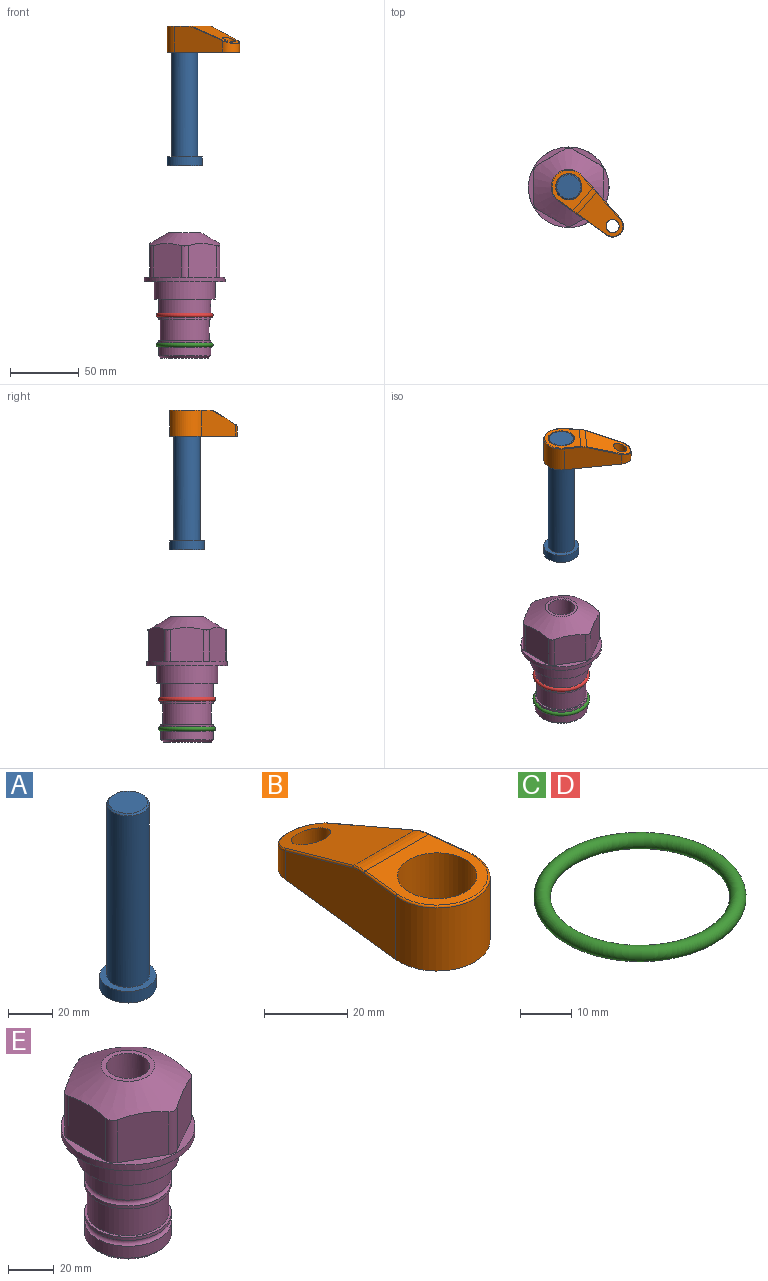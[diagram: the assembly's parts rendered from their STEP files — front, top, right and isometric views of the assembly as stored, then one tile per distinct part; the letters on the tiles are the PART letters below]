
ASSEMBLY  parts=5 mates=3
PART A: 6 faces, bbox 25.4x25.4x101.6 mm
  f0: plane 17.46x17.46mm, normal (0,0,1), area 239.5mm2, adj f5
  f1: plane 25.4x25.4mm, normal (0,0,-1), area 506.7mm2, adj f2
  f2: cylinder r=12.7mm len=25.4mm, axis (0,0,1), area 506.7mm2, adj f1,f3
  f3: plane 25.4x25.4mm, normal (0,0,1), area 221.7mm2, adj f2,f4
  f4: cylinder r=9.53mm len=94.46mm, axis (0,0,1), area 5653mm2, adj f3,f5
  f5: cone r=8.73mm half-angle=45deg, axis (0,0,-1), area 64.4mm2, adj f0,f4
PART B: 44 faces, bbox 27.5x64.5x19.1 mm
  f0: plane 2.3x0.95mm, normal (0,0,-1), area 1mm2, adj f25,f30,f34
  f1: plane 63.5x25.4mm, normal (0,0,-1), area 561.7mm2, adj f2,f3,f4,f5,f6,f7,f19,f20
  f2: cylinder r=12.7mm len=25.4mm, axis (0,0,-1), area 792.2mm2, adj f1,f3,f5,f13
  f3: plane 42.33x18.54mm, normal (0.99,0.11,0), area 647mm2, adj f1,f2,f4,f11,f12,f14
  f4: cylinder r=7.94mm len=15.78mm, axis (0,0,-1), area 158.6mm2, adj f1,f3,f5,f16
  f5: plane 42.33x18.54mm, normal (-0.99,0.11,0), area 647mm2, adj f1,f2,f4,f15,f17,f18
  f6: cylinder r=9.53mm len=19.05mm, axis (0,0,-1), area 1140.1mm2, adj f1,f8
  f7: cylinder r=4.76mm len=10.98mm, axis (0,0,-1), area 276.1mm2, adj f1,f9
  f8: plane 25.83x24.38mm, normal (0,0,1), area 262.2mm2, adj f6,f10,f11,f13,f15
  f9: plane 32.49x20.55mm, normal (0,0.34,0.94), area 489.9mm2, adj f7,f10,f14,f16,f18
  f10: cylinder r=12.7mm len=21.49mm, axis (-1,0,0), area 93.2mm2, adj f8,f9,f12,f17
  f11: cylinder r=0.51mm len=12.34mm, axis (0.11,-0.99,0), area 9.9mm2, adj f3,f8,f12,f13
  f12: bspline ~7.62x1.64mm, area 3.5mm2, adj f3,f10,f11,f14
  f13: torus R=12.19mm, axis (0,0,1), area 33.6mm2, adj f2,f8,f11,f15
  f14: cylinder r=0.51mm len=26.01mm, axis (0.1,-0.93,0.34), area 21.6mm2, adj f3,f9,f12,f16
  f15: cylinder r=0.51mm len=12.34mm, axis (0.11,0.99,0), area 9.9mm2, adj f5,f8,f13,f17
  f16: bspline ~15.78x7.05mm, area 15.7mm2, adj f4,f9,f14,f18
  f17: bspline ~7.62x1.64mm, area 3.5mm2, adj f5,f10,f15,f18
  f18: cylinder r=0.51mm len=26.01mm, axis (0.1,0.93,-0.34), area 21.6mm2, adj f5,f9,f16,f17
  f19: plane 21.6x14.29mm, normal (-0.99,-0.11,0), area 242.6mm2, adj f1,f26,f28,f34,f36,f38
  f20: plane 21.6x14.29mm, normal (0.99,-0.11,0), area 242.6mm2, adj f1,f27,f29,f37,f39,f41
  f21: cylinder r=12.7mm len=14.29mm, axis (0,0,-1), area 173.2mm2, adj f1,f26,f27,f30,f31,f33
  f22: cylinder r=7.94mm len=7.63mm, axis (0,0,-1), area 53.8mm2, adj f1,f28,f29,f42
  f23: plane 2.3x0.95mm, normal (0,0,-1), area 1mm2, adj f25,f33,f37
  f24: plane 17.94x12.32mm, normal (0,-0.34,-0.94), area 191.2mm2, adj f25,f38,f41,f42
  f25: cylinder r=9.53mm len=12.93mm, axis (-1,0,0), area 37.5mm2, adj f0,f23,f24,f31,f36,f39
  f26: cylinder r=1.59mm len=14.29mm, axis (0,0,-1), area 49mm2, adj f1,f19,f21,f32
  f27: cylinder r=1.59mm len=14.29mm, axis (0,0,-1), area 49mm2, adj f1,f20,f21,f35
  f28: cylinder r=1.59mm len=7.28mm, axis (0,0,-1), area 22.1mm2, adj f1,f19,f22,f40
  f29: cylinder r=1.59mm len=7.28mm, axis (0,0,-1), area 22.1mm2, adj f1,f20,f22,f43
  f30: torus R=14.29mm, axis (0,0,1), area 5.8mm2, adj f0,f21,f31,f32
  f31: bspline ~11.06x2.73mm, area 20.8mm2, adj f21,f25,f30,f33
  f32: sphere r=1.59mm, area 5.4mm2, adj f26,f30,f34
  f33: torus R=14.29mm, axis (0,0,1), area 5.8mm2, adj f21,f23,f31,f35
  f34: cylinder r=1.59mm len=1.68mm, axis (-0.11,0.99,0), area 2.4mm2, adj f0,f19,f32,f36
  f35: sphere r=1.59mm, area 5.4mm2, adj f27,f33,f37
  f36: bspline ~5.82x2.33mm, area 7.7mm2, adj f19,f25,f34,f38
  f37: cylinder r=1.59mm len=1.68mm, axis (0.11,0.99,0), area 2.4mm2, adj f20,f23,f35,f39
  f38: cylinder r=1.59mm len=18.33mm, axis (0.1,-0.93,0.34), area 46.7mm2, adj f19,f24,f36,f40
  f39: bspline ~5.82x2.33mm, area 7.7mm2, adj f20,f25,f37,f41
  f40: sphere r=1.59mm, area 3.6mm2, adj f28,f38,f42
  f41: cylinder r=1.59mm len=18.33mm, axis (0.1,0.93,-0.34), area 46.7mm2, adj f20,f24,f39,f43
  f42: bspline ~8.31x1.84mm, area 15.3mm2, adj f22,f24,f40,f43
  f43: sphere r=1.59mm, area 3.6mm2, adj f29,f41,f42
PART C: 1 faces, bbox 44.7x44.7x3.2 mm
  f0: torus R=19.05mm, axis (0,0,1), area 1193.9mm2
PART D: same geometry as C
PART E: 36 faces, bbox 58.7x58.7x91.2 mm
  f0: cylinder r=17.78mm len=35.56mm, axis (0,0,1), area 1670.8mm2, adj f23,f24,f31
  f1: cylinder r=19.05mm len=38.1mm, axis (0,0,1), area 1191.9mm2, adj f26,f27,f30
  f2: plane 58.66x58.66mm, normal (0,0,-1), area 1150.6mm2, adj f3,f28
  f3: cylinder r=29.33mm len=58.66mm, axis (0,0,-1), area 585.1mm2, adj f2,f4
  f4: plane 58.66x58.66mm, normal (0,0,1), area 475.9mm2, adj f3,f5,f6,f7,f8,f9,f10,f11
  f5: plane 24.5x20.32mm, normal (-0.5,0.87,0), area 562.8mm2, adj f4,f15,f16,f17
  f6: plane 24.5x20.32mm, normal (0.5,0.87,0), area 562.8mm2, adj f4,f14,f15,f17
  f7: plane 24.5x23.48mm, normal (1,0,0), area 562.8mm2, adj f4,f13,f14,f17
  f8: plane 24.5x20.32mm, normal (0.5,-0.87,0), area 562.8mm2, adj f4,f12,f13,f17
  f9: plane 24.5x20.32mm, normal (-0.5,-0.87,0), area 562.8mm2, adj f4,f11,f12,f17
  f10: plane 24.5x23.48mm, normal (-1,0,0), area 562.8mm2, adj f4,f11,f16,f17
  f11: cylinder r=5.08mm len=23.01mm, axis (0,0,-1), area 121.2mm2, adj f4,f9,f10,f17
  f12: cylinder r=5.08mm len=23.01mm, axis (0,0,-1), area 121.2mm2, adj f4,f8,f9,f17
  f13: cylinder r=5.08mm len=23.01mm, axis (0,0,-1), area 121.2mm2, adj f4,f7,f8,f17
  f14: cylinder r=5.08mm len=23.01mm, axis (0,0,-1), area 121.2mm2, adj f4,f6,f7,f17
  f15: cylinder r=5.08mm len=23.01mm, axis (0,0,-1), area 121.2mm2, adj f4,f5,f6,f17
  f16: cylinder r=5.08mm len=23.01mm, axis (0,0,-1), area 121.2mm2, adj f4,f5,f10,f17
  f17: cone r=11.73mm half-angle=60deg, axis (0,0,-1), area 2071.8mm2, adj f5,f6,f7,f8,f9,f10,f11,f12
  f18: plane 23.46x23.46mm, normal (0,0,1), area 147.4mm2, adj f17,f35
  f19: plane 34.93x34.93mm, normal (0,0,-1), area 958mm2, adj f29
  f20: cylinder r=19.05mm len=38.1mm, axis (0,0,1), area 760.1mm2, adj f21,f29
  f21: torus R=19.05mm, axis (0,0,1), area 565.3mm2, adj f20,f22
  f22: cylinder r=19.05mm len=38.1mm, axis (0,0,1), area 190mm2, adj f21,f23
  f23: plane 38.1x38.1mm, normal (0,0,1), area 146.9mm2, adj f0,f22
  f24: plane 38.1x38.1mm, normal (0,0,-1), area 146.9mm2, adj f0,f25
  f25: cylinder r=19.05mm len=38.1mm, axis (0,0,1), area 190mm2, adj f24,f26
  f26: torus R=19.05mm, axis (0,0,1), area 565.3mm2, adj f1,f25
  f27: plane 44.45x44.45mm, normal (0,0,-1), area 411.7mm2, adj f1,f28
  f28: cylinder r=22.23mm len=44.45mm, axis (0,0,1), area 1773.5mm2, adj f2,f27
  f29: cone r=19.05mm half-angle=45deg, axis (0,0,1), area 257.5mm2, adj f19,f20
  f30: cylinder r=3.17mm len=6.75mm, axis (-1,0,0), area 128mm2, adj f1,f33
  f31: cylinder r=3.17mm len=6.35mm, axis (-1,0,0), area 102.5mm2, adj f0,f33
  f32: plane 25.4x25.4mm, normal (0,0,1), area 506.7mm2, adj f33
  f33: cylinder r=12.7mm len=66.42mm, axis (0,0,-1), area 5236.2mm2, adj f30,f31,f32,f34
  f34: cone r=9.53mm half-angle=30deg, axis (0,0,-1), area 443.4mm2, adj f33,f35
  f35: cylinder r=9.53mm len=19.05mm, axis (0,0,-1), area 849mm2, adj f18,f34
PLACE A rot(axis=(0,0,-1),41.8deg) t=(0,0,112.27)mm
PLACE B rot(axis=(0,0,-1),131.8deg) t=(0,0,166.88)mm
PLACE C t=(0,0,-21.59)mm
PLACE D at identity
PLACE E at identity fixed
MATE fastened C.f0 <-> E.f0  axis (0,0,1) through (0,0,-46.1)mm
MATE cylindrical A.f2 <-> E.f0  axis (0,0,1) through (0,0,137.91)mm
MATE fastened B.f2 <-> A.f2  axis (0,0,1) through (0,0,185.93)mm
